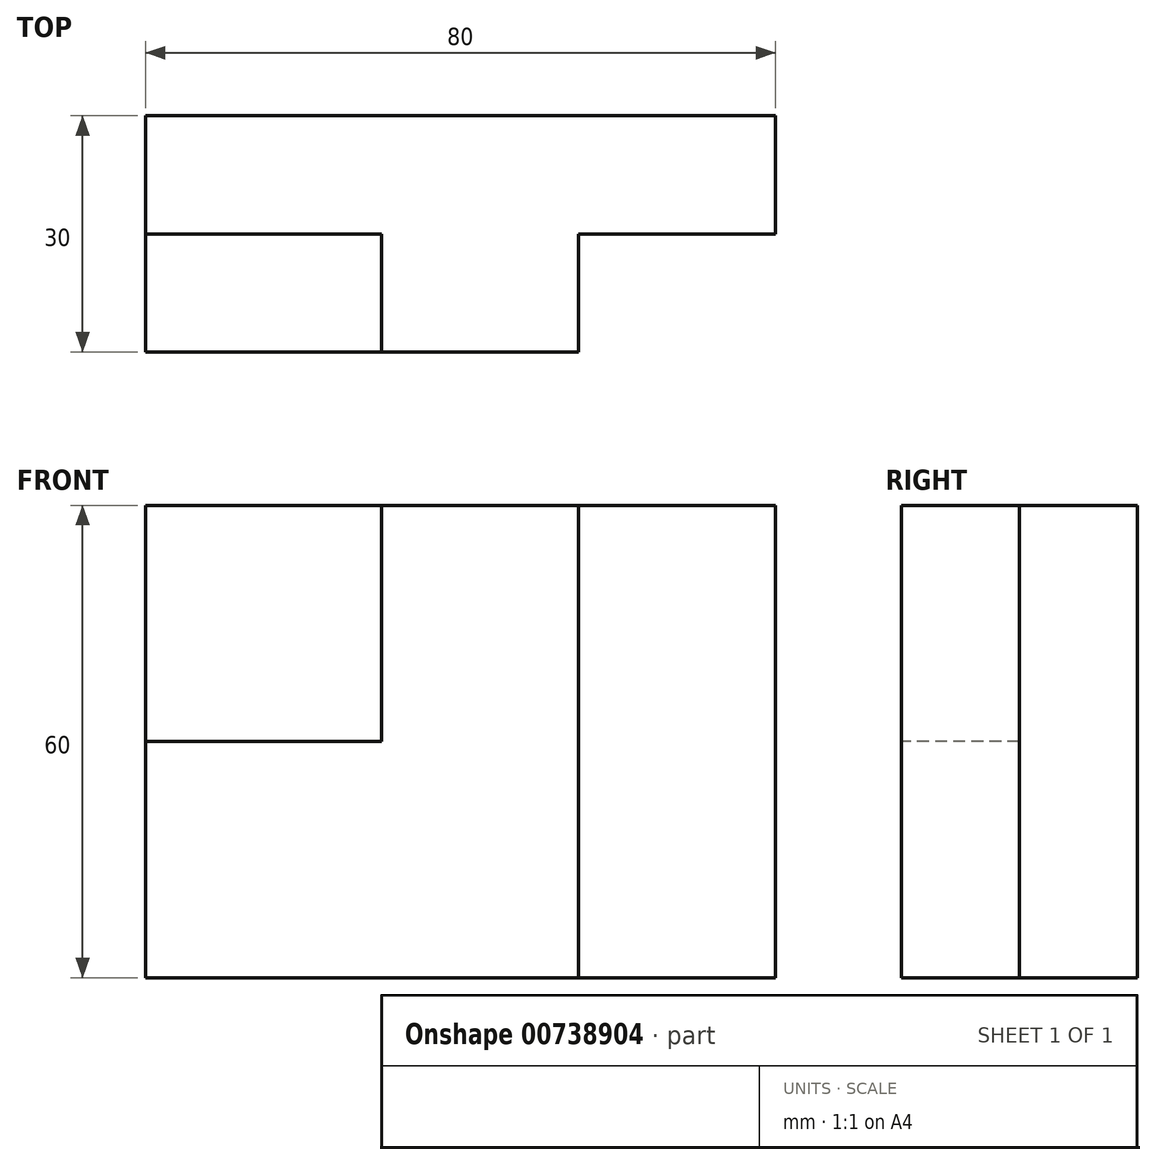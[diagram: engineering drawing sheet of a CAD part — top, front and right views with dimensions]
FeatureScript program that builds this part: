
annotation { "Feature Type Name" : "Feature", "Feature Type Description" : "" }
export const myFeature = defineFeature(function(context is Context, id is Id, definition is map)
    precondition{}
    {
        {
            var Q0;
            Q0=qCreatedBy(makeId("Front.planeOp"),FACE);
            var sketch = newSketch(context, id + "F0", { "sketchPlane" : qUnion([Q0])});
            skLineSegment(sketch, "E0.bottom", {"start": v(0, 0) * mm, "end": v(80, 0) * mm});
            skLineSegment(sketch, "E0.top", {"start": v(0, 60) * mm, "end": v(80, 60) * mm});
            skLineSegment(sketch, "E0.left", {"start": v(0, 0) * mm, "end": v(0, 60) * mm});
            skLineSegment(sketch, "E0.right", {"start": v(80, 0) * mm, "end": v(80, 60) * mm});
            skSolve(sketch);
        }
        {
            var Q0;
            Q0=makeQuery(id+"F0.imprint","IMPRINT",FACE,{"disambiguationData":[TD([[makeQuery(id+"F0.imprint","IMPRINT",EDGE,{"derivedFrom":sQuery(id+"F0.wireOp",EDGE,"E0.bottom")}),1.0]])]});
            extrude(context, id + "F1", {"entities" : qUnion([Q0]), "depth" : 30 * mm, "offsetDistance" : 25 * mm});
        }
        {
            var Q0;
            Q0=makeQuery(id+"F1.opExtrude","CAP_FACE",FACE,{"disambiguationData":[OSD([sQuery(id+"F0.wireOp",EDGE,"E0.bottom"),sQuery(id+"F0.wireOp",EDGE,"E0.top"),sQuery(id+"F0.wireOp",EDGE,"E0.left"),sQuery(id+"F0.wireOp",EDGE,"E0.right")])],"isStart":false});
            var sketch = newSketch(context, id + "F2", { "sketchPlane" : qUnion([Q0])});
            skLineSegment(sketch, "E1.bottom", {"start": v(0, 60) * mm, "end": v(30, 60) * mm});
            skLineSegment(sketch, "E1.top", {"start": v(0, 30) * mm, "end": v(30, 30) * mm});
            skLineSegment(sketch, "E1.left", {"start": v(0, 60) * mm, "end": v(0, 30) * mm});
            skLineSegment(sketch, "E1.right", {"start": v(30, 60) * mm, "end": v(30, 30) * mm});
            skLineSegment(sketch, "E2.bottom", {"start": v(80, 0) * mm, "end": v(55, 0) * mm});
            skLineSegment(sketch, "E2.top", {"start": v(80, 60) * mm, "end": v(55, 60) * mm});
            skLineSegment(sketch, "E2.left", {"start": v(80, 0) * mm, "end": v(80, 60) * mm});
            skLineSegment(sketch, "E2.right", {"start": v(55, 0) * mm, "end": v(55, 60) * mm});
            skSolve(sketch);
        }
        {
            var Q0;
            Q0=makeQuery(id+"F2.imprint","IMPRINT",FACE,{"disambiguationData":[TD([[makeQuery(id+"F2.imprint","IMPRINT",EDGE,{"derivedFrom":sQuery(id+"F2.wireOp",EDGE,"E2.bottom")}),1.0]])]});
            extrude(context, id + "F3", {"entities" : qUnion([Q0]), "operationType" : NewBodyOperationType.REMOVE, "oppositeDirection" : true, "depth" : 15 * mm, "offsetDistance" : 25 * mm});
        }
        {
            var Q0;
            Q0=makeQuery(id+"F1.opExtrude","CAP_FACE",FACE,{"disambiguationData":[OSD([sQuery(id+"F0.wireOp",EDGE,"E0.bottom"),sQuery(id+"F0.wireOp",EDGE,"E0.top"),sQuery(id+"F0.wireOp",EDGE,"E0.left"),sQuery(id+"F0.wireOp",EDGE,"E0.right")])],"isStart":false});
            var sketch = newSketch(context, id + "F4", { "sketchPlane" : qUnion([Q0])});
            skLineSegment(sketch, "E3.bottom", {"start": v(0, 60) * mm, "end": v(30, 60) * mm});
            skLineSegment(sketch, "E3.top", {"start": v(0, 30) * mm, "end": v(30, 30) * mm});
            skLineSegment(sketch, "E3.left", {"start": v(0, 60) * mm, "end": v(0, 30) * mm});
            skLineSegment(sketch, "E3.right", {"start": v(30, 60) * mm, "end": v(30, 30) * mm});
            skSolve(sketch);
        }
        {
            var Q0;
            Q0=makeQuery(id+"F4.imprint","IMPRINT",FACE,{"disambiguationData":[TD([[makeQuery(id+"F4.imprint","IMPRINT",EDGE,{"derivedFrom":sQuery(id+"F4.wireOp",EDGE,"E3.bottom")}),-1.0]])]});
            extrude(context, id + "F5", {"entities" : qUnion([Q0]), "operationType" : NewBodyOperationType.REMOVE, "oppositeDirection" : true, "depth" : 15 * mm, "offsetDistance" : 25 * mm});
        }
    });
